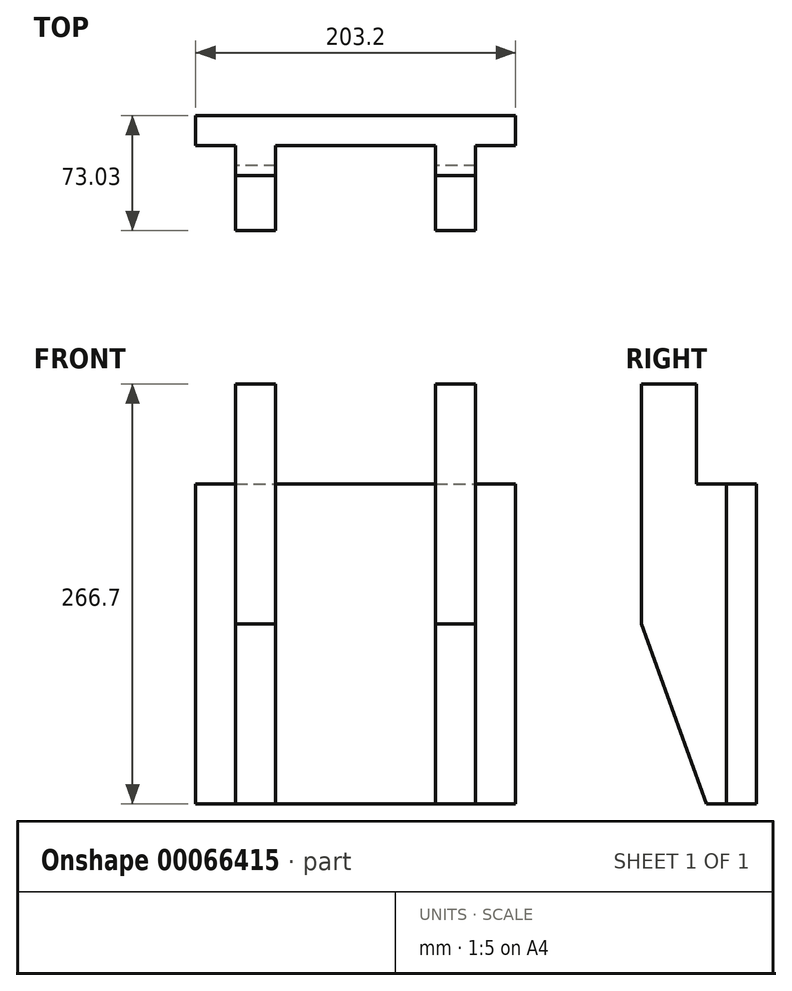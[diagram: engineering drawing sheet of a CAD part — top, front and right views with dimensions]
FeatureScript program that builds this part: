
annotation { "Feature Type Name" : "Feature", "Feature Type Description" : "" }
export const myFeature = defineFeature(function(context is Context, id is Id, definition is map)
    precondition{}
    {
        {
            var Q0;
            Q0=qCreatedBy(makeId("Front.planeOp"),FACE);
            var sketch = newSketch(context, id + "F0", { "sketchPlane" : qUnion([Q0])});
            skLineSegment(sketch, "E0.bottom", {"start": v(-101.6, 101.6) * mm, "end": v(101.6, 101.6) * mm});
            skLineSegment(sketch, "E0.top", {"start": v(-101.6, -101.6) * mm, "end": v(101.6, -101.6) * mm});
            skLineSegment(sketch, "E0.left", {"start": v(-101.6, 101.6) * mm, "end": v(-101.6, -101.6) * mm});
            skLineSegment(sketch, "E0.right", {"start": v(101.6, 101.6) * mm, "end": v(101.6, -101.6) * mm});
            skLineSegment(sketch, "E1", {"start": v(-101.6, 101.6) * mm, "end": v(101.6, -101.6) * mm, "construction": true});
            skPoint(sketch, "E2", {"position": v(0, 0) * mm});
            skSolve(sketch);
        }
        {
            var Q0;
            Q0 = qSketchRegion(id + "F0", true);
            extrude(context, id + "F1", {"entities" : qUnion([Q0]), "endBound" : BoundingType.SYMMETRIC, "depth" : 19.05 * mm});
        }
        {
            var Q0;
            Q0=qCreatedBy(makeId("Right.planeOp"),FACE);
            var sketch = newSketch(context, id + "F2", { "sketchPlane" : qUnion([Q0])});
            skLineSegment(sketch, "E3.0", {"start": v(-9.53, 101.6) * mm, "end": v(-9.53, -101.6) * mm, "construction": true});
            skLineSegment(sketch, "E4.0.0", {"start": v(9.53, -101.6) * mm, "end": v(9.53, 101.6) * mm, "construction": true});
            skLineSegment(sketch, "E4.0.3", {"start": v(-9.53, -101.6) * mm, "end": v(9.52, -101.6) * mm, "construction": true});
            skLineSegment(sketch, "E5", {"start": v(-9.53, 165.1) * mm, "end": v(-9.52, -101.6) * mm});
            skLineSegment(sketch, "E6", {"start": v(-9.53, -101.6) * mm, "end": v(-22.23, -101.6) * mm});
            skLineSegment(sketch, "E7", {"start": v(-22.22, -101.6) * mm, "end": v(-63.5, 12.7) * mm});
            skLineSegment(sketch, "E8", {"start": v(-63.5, 12.7) * mm, "end": v(-63.5, 165.1) * mm});
            skLineSegment(sketch, "E9", {"start": v(-63.5, 165.1) * mm, "end": v(-9.53, 165.1) * mm});
            skSolve(sketch);
        }
        {
            var Q0;
            Q0=makeQuery(id+"F2.imprint","IMPRINT",FACE,{"disambiguationData":[TD([[makeQuery(id+"F2.imprint","IMPRINT",EDGE,{"derivedFrom":sQuery(id+"F2.wireOp",EDGE,"E5")}),-1.0]])]});
            extrude(context, id + "F3", {"entities" : qUnion([Q0]), "operationType" : NewBodyOperationType.ADD, "endBound" : BoundingType.SYMMETRIC, "depth" : 152.4 * mm});
        }
        {
            var Q0;
            Q0=qCreatedBy(makeId("Right.planeOp"),FACE);
            var sketch = newSketch(context, id + "F4", { "sketchPlane" : qUnion([Q0])});
            skLineSegment(sketch, "E10.bottom", {"start": v(-28.57, 165.1) * mm, "end": v(9.52, 165.1) * mm});
            skLineSegment(sketch, "E10.top", {"start": v(-28.57, 101.6) * mm, "end": v(9.52, 101.6) * mm});
            skLineSegment(sketch, "E10.left", {"start": v(-28.57, 165.1) * mm, "end": v(-28.57, 101.6) * mm});
            skLineSegment(sketch, "E10.right", {"start": v(9.52, 165.1) * mm, "end": v(9.52, 101.6) * mm});
            skLineSegment(sketch, "E11.0", {"start": v(9.53, 101.6) * mm, "end": v(9.53, -101.6) * mm, "construction": true});
            skSolve(sketch);
        }
        {
            var Q0;
            Q0 = qSketchRegion(id + "F4", true);
            extrude(context, id + "F5", {"entities" : qUnion([Q0]), "operationType" : NewBodyOperationType.REMOVE, "endBound" : BoundingType.SYMMETRIC, "oppositeDirection" : true, "depth" : 203.2 * mm});
        }
        {
            var Q0;
            Q0=makeQuery(id+"F3.opExtrude","SWEPT_FACE",FACE,{"disambiguationData":[OSD([sQuery(id+"F2.wireOp",EDGE,"E8")])]});
            var sketch = newSketch(context, id + "F6", { "sketchPlane" : qUnion([Q0])});
            skLineSegment(sketch, "E12.bottom", {"start": v(-50.8, 177.8) * mm, "end": v(50.8, 177.8) * mm});
            skLineSegment(sketch, "E12.top", {"start": v(-50.8, -177.8) * mm, "end": v(50.8, -177.8) * mm});
            skLineSegment(sketch, "E12.left", {"start": v(-50.8, 177.8) * mm, "end": v(-50.8, -177.8) * mm});
            skLineSegment(sketch, "E12.right", {"start": v(50.8, 177.8) * mm, "end": v(50.8, -177.8) * mm});
            skLineSegment(sketch, "E13", {"start": v(-50.8, 177.8) * mm, "end": v(50.8, -177.8) * mm, "construction": true});
            skPoint(sketch, "E14", {"position": v(0, 0) * mm});
            skLineSegment(sketch, "E15.0", {"start": v(76.2, 12.7) * mm, "end": v(-76.2, 12.7) * mm, "construction": true});
            skLineSegment(sketch, "E15.1", {"start": v(76.2, 165.1) * mm, "end": v(-76.2, 165.1) * mm, "construction": true});
            skSolve(sketch);
        }
        {
            var Q0;
            {var subQ0=sQuery(id+"F6.wireOp",EDGE,"E12.top");Q0=makeQuery(id+"F6.imprint","IMPRINT",FACE,{"disambiguationData":[TD([[makeQuery(id+"F6.imprint","IMPRINT",EDGE,{"derivedFrom":subQ0}),1.0]])]});}
            var Q1;
            {var subQ0=sQuery(id+"F6.wireOp",EDGE,"E12.left");var subQ1=sQuery(id+"F2.wireOp",EDGE,"E8");var subQ2=makeQuery(id+"F3.opExtrude","SWEPT_EDGE",EDGE,{"disambiguationData":[OSD([subQ1,sQuery(id+"F2.wireOp",EDGE,"E9")])]});var subQ3=makeQuery(id+"F6.imprint","INTERSECT",VERTEX,{"derivedFrom":[subQ2,subQ0]});Q1=makeQuery(id+"F6.imprint","IMPRINT",FACE,{"disambiguationData":[TD([[makeQuery(id+"F6.imprint","IMPRINT",EDGE,{"disambiguationData":[TD([[subQ3,-1.0]])],"derivedFrom":subQ0}),1.0]])]});}
            var Q2;
            {var subQ0=sQuery(id+"F0.wireOp",EDGE,"E0.left");var subQ3=sQuery(id+"F0.wireOp",EDGE,"E0.top");var subQ4=sQuery(id+"F0.wireOp",EDGE,"E0.bottom");Q2=makeQuery(id+"F3.boolean.opBoolean","SPLIT",FACE,{"disambiguationData":[TD([makeQuery(id+"F1.opExtrude","SWEPT_FACE",FACE,{"disambiguationData":[OSD([subQ0])]})])],"derivedFrom":makeQuery(id+"F1.opExtrude","CAP_FACE",FACE,{"disambiguationData":[OSD([subQ4,subQ3,subQ0,sQuery(id+"F0.wireOp",EDGE,"E0.right")])],"isStart":false})});}
            extrude(context, id + "F7", {"entities" : qUnion([Q0, Q1]), "operationType" : NewBodyOperationType.REMOVE, "endBound" : BoundingType.UP_TO_SURFACE, "oppositeDirection" : true, "endBoundEntityFace" : qUnion([Q2]), "depth" : 25.4 * mm});
        }
    });
